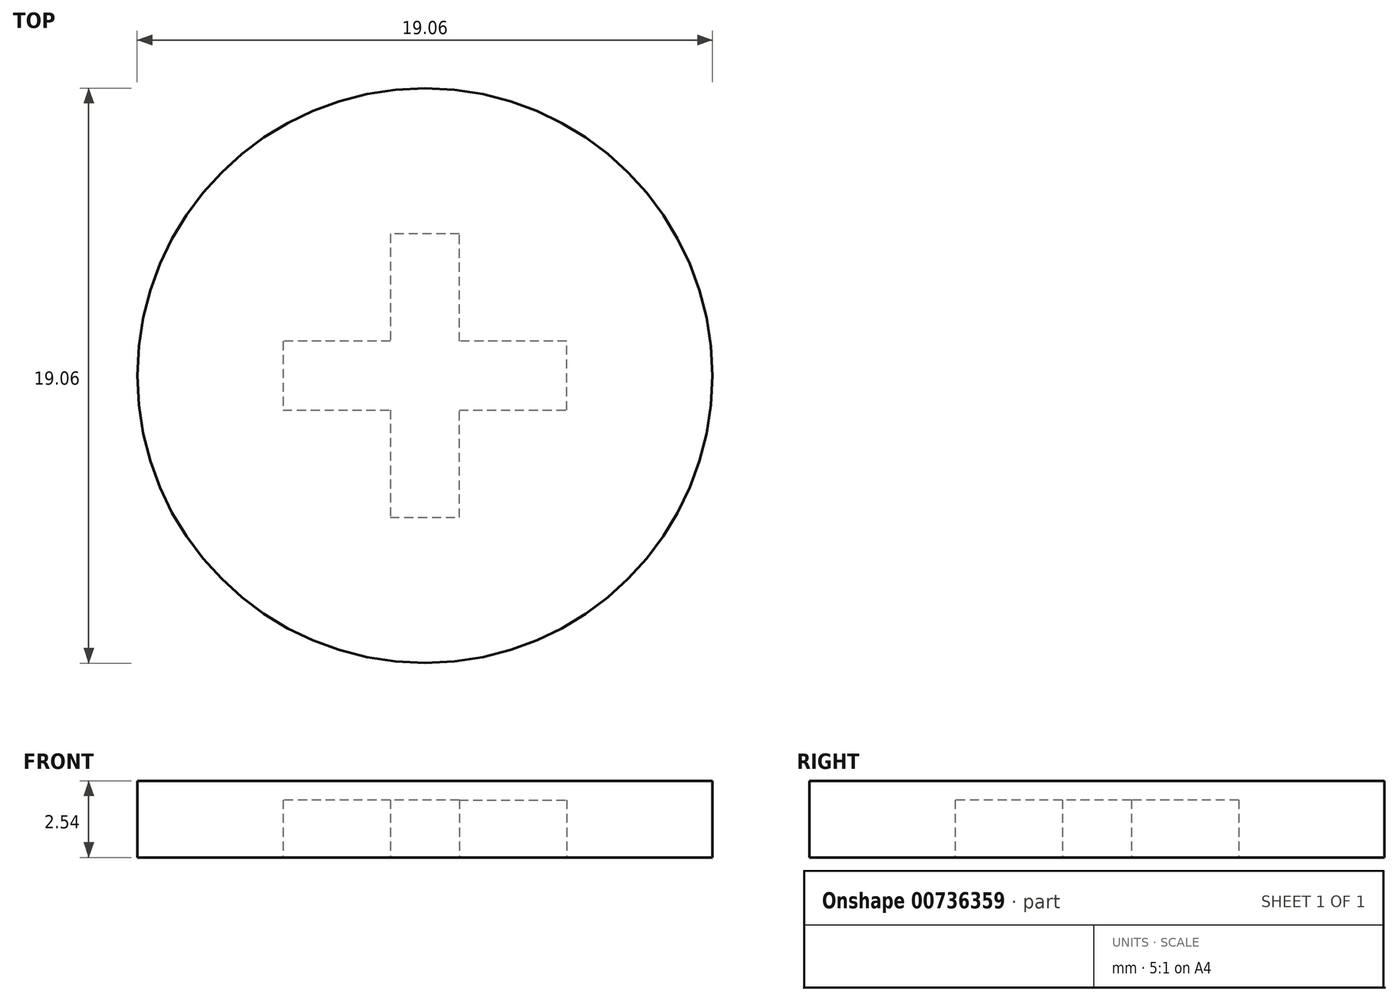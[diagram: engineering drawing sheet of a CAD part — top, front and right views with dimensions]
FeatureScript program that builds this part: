
annotation { "Feature Type Name" : "Feature", "Feature Type Description" : "" }
export const myFeature = defineFeature(function(context is Context, id is Id, definition is map)
    precondition{}
    {
        {
            var Q0;
            Q0=qCreatedBy(makeId("Top.planeOp"),FACE);
            var sketch = newSketch(context, id + "F0", { "sketchPlane" : qUnion([Q0])});
            skCircle(sketch, "E0", {"center": v(0, 0) * mm, "radius": 9.53 * mm});
            skSolve(sketch);
        }
        {
            var Q0;
            Q0 = qSketchRegion(id + "F0", true);
            extrude(context, id + "F1", {"entities" : qUnion([Q0]), "depth" : 2.54 * mm, "offsetDistance" : 25.4 * mm});
        }
        {
            var Q0;
            Q0=qCreatedBy(makeId("Top.planeOp"),FACE);
            var sketch = newSketch(context, id + "F2", { "sketchPlane" : qUnion([Q0])});
            skLineSegment(sketch, "E1", {"start": v(-1.14, 4.7) * mm, "end": v(-1.14, 1.14) * mm});
            skLineSegment(sketch, "E2", {"start": v(-1.14, 1.14) * mm, "end": v(-4.7, 1.14) * mm});
            skLineSegment(sketch, "E3", {"start": v(-4.7, 1.14) * mm, "end": v(-4.7, -1.14) * mm});
            skLineSegment(sketch, "E4", {"start": v(-4.7, -1.14) * mm, "end": v(-1.14, -1.14) * mm});
            skLineSegment(sketch, "E5", {"start": v(-1.14, -1.14) * mm, "end": v(-1.14, -4.7) * mm});
            skLineSegment(sketch, "E6", {"start": v(-1.14, -4.7) * mm, "end": v(1.14, -4.7) * mm});
            skLineSegment(sketch, "E7", {"start": v(1.14, -4.7) * mm, "end": v(1.14, -1.14) * mm});
            skLineSegment(sketch, "E8", {"start": v(1.14, -1.14) * mm, "end": v(4.7, -1.14) * mm});
            skLineSegment(sketch, "E9", {"start": v(4.7, -1.14) * mm, "end": v(4.7, 1.14) * mm});
            skLineSegment(sketch, "E10", {"start": v(4.7, 1.14) * mm, "end": v(1.14, 1.14) * mm});
            skLineSegment(sketch, "E11", {"start": v(1.14, 1.14) * mm, "end": v(1.14, 4.7) * mm});
            skLineSegment(sketch, "E12", {"start": v(1.14, 4.7) * mm, "end": v(-1.14, 4.7) * mm});
            skLineSegment(sketch, "E13", {"start": v(0, -4.7) * mm, "end": v(0, 4.7) * mm, "construction": true});
            skLineSegment(sketch, "E14", {"start": v(-4.7, 0) * mm, "end": v(4.7, 0) * mm, "construction": true});
            skSolve(sketch);
        }
        {
            var Q0;
            Q0 = qSketchRegion(id + "F2", true);
            var Q1;
            Q1=sQuery(id+"F2.wireOp",EDGE,"E1");
            var Q2;
            Q2=sQuery(id+"F2.wireOp",EDGE,"E2");
            var Q3;
            Q3=sQuery(id+"F2.wireOp",EDGE,"E3");
            var Q4;
            Q4=sQuery(id+"F2.wireOp",EDGE,"E4");
            var Q5;
            Q5=sQuery(id+"F2.wireOp",EDGE,"E5");
            var Q6;
            Q6=sQuery(id+"F2.wireOp",EDGE,"E6");
            var Q7;
            Q7=sQuery(id+"F2.wireOp",EDGE,"E7");
            var Q8;
            Q8=sQuery(id+"F2.wireOp",EDGE,"E8");
            var Q9;
            Q9=sQuery(id+"F2.wireOp",EDGE,"E9");
            var Q10;
            Q10=sQuery(id+"F2.wireOp",EDGE,"E10");
            var Q11;
            Q11=sQuery(id+"F2.wireOp",EDGE,"E11");
            var Q12;
            Q12=sQuery(id+"F2.wireOp",EDGE,"E12");
            extrude(context, id + "F3", {"entities" : qUnion([Q0]), "operationType" : NewBodyOperationType.REMOVE, "surfaceEntities" : qUnion([Q1, Q2, Q3, Q4, Q5, Q6, Q7, Q8, Q9, Q10, Q11, Q12]), "depth" : 1.9 * mm, "offsetDistance" : 25.4 * mm});
        }
    });
